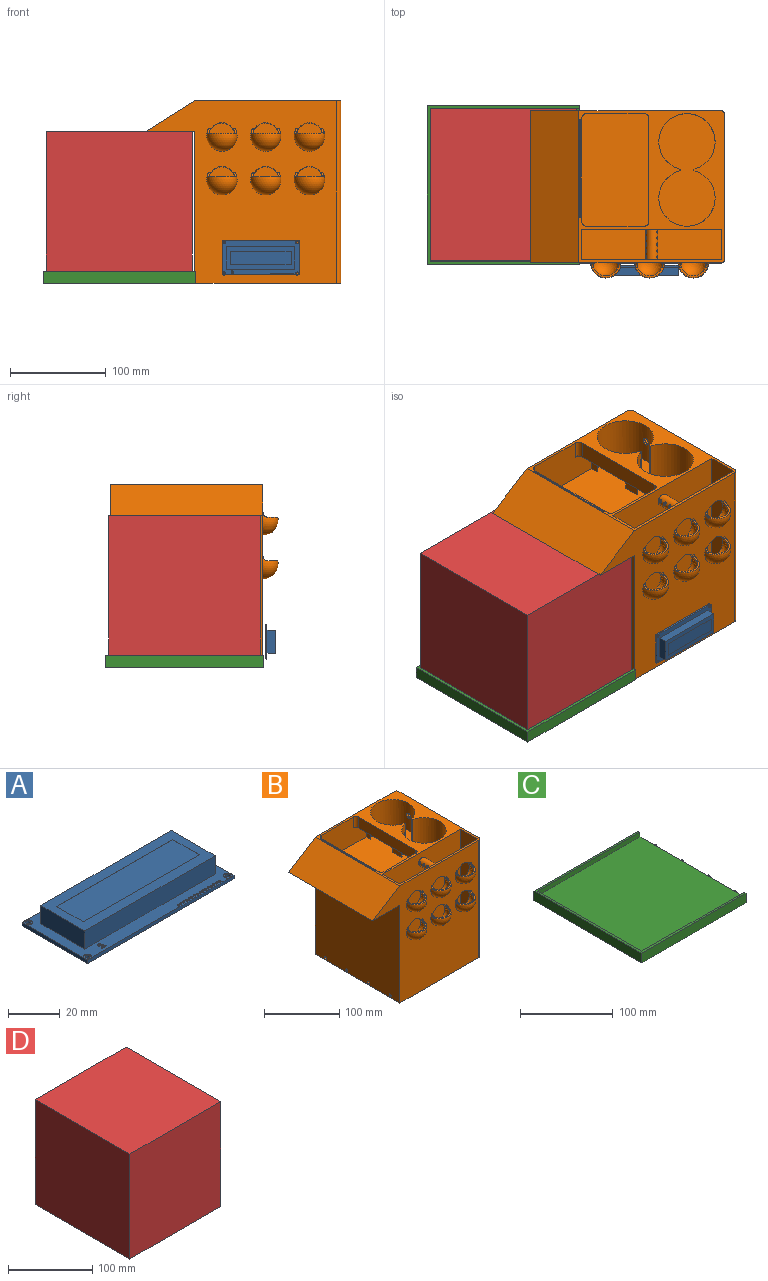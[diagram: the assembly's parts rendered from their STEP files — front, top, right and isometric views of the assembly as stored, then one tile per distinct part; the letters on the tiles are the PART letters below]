
ASSEMBLY  parts=4 mates=5
PART A: 160 faces, bbox 80.1x35.8x10.3 mm
  f0: plane 80.1x35.7mm, normal (0,0,1), area 1082mm2, adj f3,f4,f5,f6,f8,f9,f10,f11
  f1: plane 1.53x1.01mm, normal (0,0,1), area 0.4mm2, adj f5,f6,f22
  f2: plane 1.67x1.67mm, normal (0,0,1), area 0.6mm2, adj f4,f5,f18
  f3: plane 35.7x1.7mm, normal (1,0,0), area 60.7mm2, adj f0,f4,f6,f7
  f4: plane 80.1x1.7mm, normal (0,1,0), area 136.2mm2, adj f0,f2,f3,f5,f7
  f5: plane 35.7x1.7mm, normal (-1,0,0), area 60.7mm2, adj f0,f1,f2,f4,f6,f7
  f6: plane 80.1x1.7mm, normal (0,-1,0), area 136.2mm2, adj f0,f1,f3,f5,f7,f21,f26,f32
  f7: plane 80.1x35.7mm, normal (0,0,-1), area 2844.4mm2, adj f3,f4,f5,f6,f20,f29,f30,f31
  f8: plane 24x8.6mm, normal (1,0,0), area 206.4mm2, adj f0,f9,f11,f12
  f9: plane 71.2x8.6mm, normal (0,1,0), area 612.3mm2, adj f0,f8,f10,f12
  f10: plane 24x8.6mm, normal (-1,0,0), area 206.4mm2, adj f0,f9,f11,f12
  f11: plane 71.2x8.6mm, normal (0,-1,0), area 612.3mm2, adj f0,f8,f10,f12
  f12: plane 71.2x24mm, normal (0,0,1), area 802.2mm2, adj f8,f9,f10,f11,f13,f14,f15,f16
  f13: plane 14.3x0.05mm, normal (-1,0,0), area 0.7mm2, adj f12,f14,f16,f17
  f14: plane 63.4x0.05mm, normal (0,1,0), area 3.2mm2, adj f12,f13,f15,f17
  f15: plane 14.3x0.05mm, normal (1,0,0), area 0.7mm2, adj f12,f14,f16,f17
  f16: plane 63.4x0.05mm, normal (0,-1,0), area 3.2mm2, adj f12,f13,f15,f17
  f17: plane 63.4x14.3mm, normal (0,0,1), area 906.6mm2, adj f13,f14,f15,f16
  f18: cylinder r=1.67mm len=3.34mm, axis (0,0,-1), area 0mm2, adj f0,f2,f19
  f19: plane 3.34x3.34mm, normal (0,0,1), area 6mm2, adj f18,f20
  f20: cylinder r=0.94mm len=1.88mm, axis (0,0,1), area 10mm2, adj f7,f19
  f21: plane 1.33x0.14mm, normal (0,0,-1), area 0.1mm2, adj f6,f22
  f22: cylinder r=1.67mm len=3.34mm, axis (0,0,-1), area 0mm2, adj f0,f1,f21,f23
  f23: plane 3.34x3.34mm, normal (0,0,1), area 6mm2, adj f22,f29
  f24: cylinder r=1.67mm len=3.34mm, axis (0,0,-1), area 0mm2, adj f0,f25
  f25: plane 3.34x3.34mm, normal (0,0,1), area 6mm2, adj f24,f30
  f26: plane 1.33x0.14mm, normal (0,0,-1), area 0.1mm2, adj f6,f27
  f27: cylinder r=1.67mm len=3.34mm, axis (0,0,-1), area 0mm2, adj f0,f26,f28
  f28: plane 3.34x3.34mm, normal (0,0,1), area 6mm2, adj f27,f31
  f29: cylinder r=0.94mm len=1.88mm, axis (0,0,1), area 10mm2, adj f7,f23
  f30: cylinder r=0.94mm len=1.88mm, axis (0,0,1), area 10mm2, adj f7,f25
  f31: cylinder r=0.94mm len=1.88mm, axis (0,0,1), area 10mm2, adj f7,f28
  f32: plane 1.19x0mm, normal (1,0,0), area 0mm2, adj f0,f6,f33,f35
  f33: cylinder r=0.53mm len=1.06mm, axis (0,0,-1), area 0mm2, adj f0,f32,f34,f35
  f34: plane 1.19x0mm, normal (-1,0,0), area 0mm2, adj f0,f6,f33,f35
  f35: plane 1.72x1.06mm, normal (0,0,1), area 1.4mm2, adj f6,f32,f33,f34,f36
  f36: cylinder r=0.29mm len=1.7mm, axis (0,0,1), area 3.1mm2, adj f7,f35
  f37: plane 1.19x0mm, normal (1,0,0), area 0mm2, adj f0,f6,f38,f40
  f38: cylinder r=0.53mm len=1.06mm, axis (0,0,-1), area 0mm2, adj f0,f37,f39,f40
  f39: plane 1.19x0mm, normal (-1,0,0), area 0mm2, adj f0,f6,f38,f40
  f40: plane 1.72x1.06mm, normal (0,0,1), area 1.4mm2, adj f6,f37,f38,f39,f97
  f41: plane 1.19x0mm, normal (1,0,0), area 0mm2, adj f0,f6,f42,f44
  f42: cylinder r=0.53mm len=1.06mm, axis (0,0,-1), area 0mm2, adj f0,f41,f43,f44
  f43: plane 1.19x0mm, normal (-1,0,0), area 0mm2, adj f0,f6,f42,f44
  f44: plane 1.72x1.06mm, normal (0,0,1), area 1.4mm2, adj f6,f41,f42,f43,f98
  f45: plane 1.19x0mm, normal (1,0,0), area 0mm2, adj f0,f6,f46,f48
  f46: cylinder r=0.53mm len=1.06mm, axis (0,0,-1), area 0mm2, adj f0,f45,f47,f48
  f47: plane 1.19x0mm, normal (-1,0,0), area 0mm2, adj f0,f6,f46,f48
  f48: plane 1.72x1.06mm, normal (0,0,1), area 1.4mm2, adj f6,f45,f46,f47,f99
  f49: plane 1.19x0mm, normal (1,0,0), area 0mm2, adj f0,f6,f50,f52
  f50: cylinder r=0.53mm len=1.06mm, axis (0,0,-1), area 0mm2, adj f0,f49,f51,f52
  f51: plane 1.19x0mm, normal (-1,0,0), area 0mm2, adj f0,f6,f50,f52
  f52: plane 1.72x1.06mm, normal (0,0,1), area 1.4mm2, adj f6,f49,f50,f51,f100
  f53: plane 1.19x0mm, normal (1,0,0), area 0mm2, adj f0,f6,f54,f56
  f54: cylinder r=0.53mm len=1.06mm, axis (0,0,-1), area 0mm2, adj f0,f53,f55,f56
  f55: plane 1.19x0mm, normal (-1,0,0), area 0mm2, adj f0,f6,f54,f56
  f56: plane 1.72x1.06mm, normal (0,0,1), area 1.4mm2, adj f6,f53,f54,f55,f101
  f57: plane 1.19x0mm, normal (1,0,0), area 0mm2, adj f0,f6,f58,f60
  f58: cylinder r=0.53mm len=1.06mm, axis (0,0,-1), area 0mm2, adj f0,f57,f59,f60
  f59: plane 1.19x0mm, normal (-1,0,0), area 0mm2, adj f0,f6,f58,f60
  f60: plane 1.72x1.06mm, normal (0,0,1), area 1.4mm2, adj f6,f57,f58,f59,f102
  f61: plane 1.19x0mm, normal (1,0,0), area 0mm2, adj f0,f6,f62,f64
  f62: cylinder r=0.53mm len=1.06mm, axis (0,0,-1), area 0mm2, adj f0,f61,f63,f64
  f63: plane 1.19x0mm, normal (-1,0,0), area 0mm2, adj f0,f6,f62,f64
  f64: plane 1.72x1.06mm, normal (0,0,1), area 1.4mm2, adj f6,f61,f62,f63,f103
  f65: plane 1.19x0mm, normal (1,0,0), area 0mm2, adj f0,f6,f66,f68
  f66: cylinder r=0.53mm len=1.06mm, axis (0,0,-1), area 0mm2, adj f0,f65,f67,f68
  f67: plane 1.19x0mm, normal (-1,0,0), area 0mm2, adj f0,f6,f66,f68
  f68: plane 1.72x1.06mm, normal (0,0,1), area 1.4mm2, adj f6,f65,f66,f67,f104
  f69: plane 1.19x0mm, normal (1,0,0), area 0mm2, adj f0,f6,f70,f72
  f70: cylinder r=0.53mm len=1.06mm, axis (0,0,-1), area 0mm2, adj f0,f69,f71,f72
  f71: plane 1.19x0mm, normal (-1,0,0), area 0mm2, adj f0,f6,f70,f72
  f72: plane 1.72x1.06mm, normal (0,0,1), area 1.4mm2, adj f6,f69,f70,f71,f105
  f73: plane 1.19x0mm, normal (1,0,0), area 0mm2, adj f0,f6,f74,f76
  f74: cylinder r=0.53mm len=1.06mm, axis (0,0,-1), area 0mm2, adj f0,f73,f75,f76
  f75: plane 1.19x0mm, normal (-1,0,0), area 0mm2, adj f0,f6,f74,f76
  f76: plane 1.72x1.06mm, normal (0,0,1), area 1.4mm2, adj f6,f73,f74,f75,f106
  f77: plane 1.19x0mm, normal (1,0,0), area 0mm2, adj f0,f6,f78,f80
  f78: cylinder r=0.53mm len=1.06mm, axis (0,0,-1), area 0mm2, adj f0,f77,f79,f80
  f79: plane 1.19x0mm, normal (-1,0,0), area 0mm2, adj f0,f6,f78,f80
  f80: plane 1.72x1.06mm, normal (0,0,1), area 1.4mm2, adj f6,f77,f78,f79,f107
  f81: plane 1.19x0mm, normal (1,0,0), area 0mm2, adj f0,f6,f82,f84
  f82: cylinder r=0.53mm len=1.06mm, axis (0,0,-1), area 0mm2, adj f0,f81,f83,f84
  f83: plane 1.19x0mm, normal (-1,0,0), area 0mm2, adj f0,f6,f82,f84
  f84: plane 1.72x1.06mm, normal (0,0,1), area 1.4mm2, adj f6,f81,f82,f83,f108
  f85: plane 1.19x0mm, normal (1,0,0), area 0mm2, adj f0,f6,f86,f88
  f86: cylinder r=0.53mm len=1.06mm, axis (0,0,-1), area 0mm2, adj f0,f85,f87,f88
  f87: plane 1.19x0mm, normal (-1,0,0), area 0mm2, adj f0,f6,f86,f88
  f88: plane 1.72x1.06mm, normal (0,0,1), area 1.4mm2, adj f6,f85,f86,f87,f109
  f89: plane 1.19x0mm, normal (1,0,0), area 0mm2, adj f0,f6,f90,f92
  f90: cylinder r=0.53mm len=1.06mm, axis (0,0,-1), area 0mm2, adj f0,f89,f91,f92
  f91: plane 1.19x0mm, normal (-1,0,0), area 0mm2, adj f0,f6,f90,f92
  f92: plane 1.72x1.06mm, normal (0,0,1), area 1.4mm2, adj f6,f89,f90,f91,f110
  f93: plane 1.19x0mm, normal (1,0,0), area 0mm2, adj f0,f6,f94,f96
  f94: cylinder r=0.53mm len=1.06mm, axis (0,0,-1), area 0mm2, adj f0,f93,f95,f96
  f95: plane 1.19x0mm, normal (-1,0,0), area 0mm2, adj f0,f6,f94,f96
  f96: plane 1.72x1.06mm, normal (0,0,1), area 1.4mm2, adj f6,f93,f94,f95,f111
  f97: cylinder r=0.29mm len=1.7mm, axis (0,0,1), area 3.1mm2, adj f7,f40
  f98: cylinder r=0.29mm len=1.7mm, axis (0,0,1), area 3.1mm2, adj f7,f44
  f99: cylinder r=0.29mm len=1.7mm, axis (0,0,1), area 3.1mm2, adj f7,f48
  f100: cylinder r=0.29mm len=1.7mm, axis (0,0,1), area 3.1mm2, adj f7,f52
  f101: cylinder r=0.29mm len=1.7mm, axis (0,0,1), area 3.1mm2, adj f7,f56
  f102: cylinder r=0.29mm len=1.7mm, axis (0,0,1), area 3.1mm2, adj f7,f60
  f103: cylinder r=0.29mm len=1.7mm, axis (0,0,1), area 3.1mm2, adj f7,f64
  f104: cylinder r=0.29mm len=1.7mm, axis (0,0,1), area 3.1mm2, adj f7,f68
  f105: cylinder r=0.29mm len=1.7mm, axis (0,0,1), area 3.1mm2, adj f7,f72
  f106: cylinder r=0.29mm len=1.7mm, axis (0,0,1), area 3.1mm2, adj f7,f76
  f107: cylinder r=0.29mm len=1.7mm, axis (0,0,1), area 3.1mm2, adj f7,f80
  f108: cylinder r=0.29mm len=1.7mm, axis (0,0,1), area 3.1mm2, adj f7,f84
  f109: cylinder r=0.29mm len=1.7mm, axis (0,0,1), area 3.1mm2, adj f7,f88
  f110: cylinder r=0.29mm len=1.7mm, axis (0,0,1), area 3.1mm2, adj f7,f92
  f111: cylinder r=0.29mm len=1.7mm, axis (0,0,1), area 3.1mm2, adj f7,f96
  f112: cylinder r=0.46mm len=0.14mm, axis (0,0,-1), area 0mm2, adj f113,f155,f156,f159
  f113: cylinder r=0.42mm len=0.18mm, axis (0,0,-1), area 0mm2, adj f112,f114,f156,f159
  f114: cylinder r=1.01mm len=0.33mm, axis (0,0,-1), area 0mm2, adj f113,f115,f156,f159
  f115: plane 0.11x0.1mm, normal (0.38,0.93,0), area 0mm2, adj f114,f116,f156,f159
  f116: plane 0.43x0.16mm, normal (-0.93,0.36,0), area 0mm2, adj f115,f117,f156,f159
  f117: plane 0.47x0.15mm, normal (-0.95,0.31,0), area 0mm2, adj f116,f118,f156,f159
  f118: cylinder r=0.82mm len=0.1mm, axis (0,0,-1), area 0mm2, adj f117,f119,f156,f159
  f119: cylinder r=0.71mm len=0.28mm, axis (0,0,-1), area 0mm2, adj f118,f120,f156,f159
  f120: extruded ~0.37x0.11mm, area 0mm2, adj f119,f155,f156,f159
  f121: extruded ~0.17x0.1mm, area 0mm2, adj f122,f152,f156,f158
  f122: plane 0.49x0.18mm, normal (0.94,-0.34,0), area 0.1mm2, adj f121,f123,f156,f158
  f123: cylinder r=0.59mm len=0.12mm, axis (0,0,-1), area 0mm2, adj f122,f152,f156,f158
  f124: cylinder r=2.75mm len=0.28mm, axis (0,0,1), area 0mm2, adj f125,f153,f156,f157
  f125: cylinder r=1.46mm len=0.25mm, axis (0,0,1), area 0mm2, adj f124,f126,f156,f157
  f126: cylinder r=0.53mm len=0.1mm, axis (0,0,1), area 0mm2, adj f125,f127,f156,f157
  f127: plane 1.13x0.34mm, normal (0.96,0.29,0), area 0.1mm2, adj f126,f128,f156,f157
  f128: plane 0.75x0.31mm, normal (-0.92,0.38,0), area 0.1mm2, adj f127,f153,f156,f157
  f129: plane 0.2x0.1mm, normal (0.92,-0.39,0), area 0mm2, adj f0,f130,f154,f156
  f130: extruded ~0.32x0.26mm, area 0mm2, adj f0,f129,f131,f156
  f131: extruded ~0.31x0.25mm, area 0mm2, adj f0,f130,f132,f156
  f132: plane 2.73x0.95mm, normal (-0.94,-0.33,0), area 0.3mm2, adj f0,f131,f133,f156
  f133: plane 0.1x0.04mm, normal (-0.97,-0.23,0), area 0mm2, adj f0,f132,f134,f156
  f134: extruded ~0.14x0.11mm, area 0mm2, adj f0,f133,f135,f156
  f135: cylinder r=0.51mm len=0.24mm, axis (0,0,1), area 0mm2, adj f0,f134,f136,f156
  f136: extruded ~0.19x0.1mm, area 0mm2, adj f0,f135,f137,f156
  f137: plane 0.58x0.2mm, normal (0.94,0.33,0), area 0.1mm2, adj f0,f136,f138,f156
  f138: plane 0.1x0.03mm, normal (-1,-0.04,0), area 0mm2, adj f0,f137,f139,f156
  f139: extruded ~0.63x0.25mm, area 0.1mm2, adj f0,f138,f140,f156
  f140: extruded ~0.67x0.22mm, area 0.1mm2, adj f0,f139,f141,f156
  f141: extruded ~0.63x0.15mm, area 0.1mm2, adj f0,f140,f142,f156
  f142: cylinder r=0.76mm len=0.18mm, axis (0,0,1), area 0mm2, adj f0,f141,f143,f156
  f143: plane 0.1x0.01mm, normal (0.46,0.89,0), area 0mm2, adj f0,f142,f144,f156
  f144: extruded ~0.13x0.1mm, area 0mm2, adj f0,f143,f145,f156
  f145: plane 0.1x0.04mm, normal (0.99,-0.13,0), area 0mm2, adj f0,f144,f146,f156
  f146: plane 1.11x0.41mm, normal (0.94,-0.34,0), area 0.1mm2, adj f0,f145,f147,f156
  f147: cylinder r=0.89mm len=0.17mm, axis (0,0,1), area 0mm2, adj f0,f146,f148,f156
  f148: extruded ~0.44x0.14mm, area 0mm2, adj f0,f147,f149,f156
  f149: cylinder r=0.76mm len=0.37mm, axis (0,0,1), area 0mm2, adj f0,f148,f150,f156
  f150: cylinder r=0.6mm len=0.24mm, axis (0,0,1), area 0mm2, adj f0,f149,f151,f156
  f151: cylinder r=1.08mm len=0.3mm, axis (0,0,1), area 0mm2, adj f0,f150,f154,f156
  f152: cylinder r=0.32mm len=0.27mm, axis (0,0,-1), area 0mm2, adj f121,f123,f156,f158
  f153: plane 0.1x0.04mm, normal (-0.36,-0.93,0), area 0mm2, adj f124,f128,f156,f157
  f154: cylinder r=1.34mm len=0.2mm, axis (0,0,1), area 0mm2, adj f0,f129,f151,f156
  f155: extruded ~0.32x0.14mm, area 0mm2, adj f112,f120,f156,f159
  f156: plane 3.41x2.58mm, normal (0,0,1), area 4.8mm2, adj f112,f113,f114,f115,f116,f117,f118,f119
  f157: plane 1.13x0.65mm, normal (0,0,1), area 0.3mm2, adj f124,f125,f126,f127,f128,f153
  f158: plane 0.49x0.26mm, normal (0,0,1), area 0.1mm2, adj f121,f122,f123,f152
  f159: plane 0.99x0.89mm, normal (0,0,1), area 0.6mm2, adj f112,f113,f114,f115,f116,f117,f118,f119
PART B: 95 faces, bbox 203.2x174.6x190.5 mm
  f0: cylinder r=3.91mm len=7.83mm, axis (1,0,0), area 67.5mm2, adj f6,f93
  f1: plane 158.75x152.4mm, normal (0,0,1), area 5716.6mm2, adj f4,f6,f7,f8,f9,f10,f13,f14
  f2: cylinder r=6.23mm len=32mm, axis (0,1,0), area 1089.1mm2, adj f4,f13,f33,f34,f35,f36,f37,f38
  f3: cylinder r=4.95mm len=38.1mm, axis (0,-1,0), area 1046.4mm2, adj f5,f19,f23,f28,f31,f32,f33,f34
  f4: plane 152.4x146.3mm, normal (0,-1,0), area 22174.8mm2, adj f1,f2,f14,f15,f16
  f5: plane 3.53x1.42mm, normal (0,0,-1), area 1.6mm2, adj f3,f19,f28
  f6: cylinder r=29.4mm len=58.8mm, axis (0,0,1), area 6258.3mm2, adj f0,f1,f17,f18,f23,f24,f25,f94
  f7: cylinder r=29.4mm len=58.8mm, axis (0,0,1), area 6306.6mm2, adj f1,f17,f18,f23,f24,f26,f94
  f8: plane 198.63x190.5mm, normal (0,-1,0), area 24579.4mm2, adj f1,f11,f12,f51,f52,f53,f54,f55
  f9: plane 190.5x149.61mm, normal (1,0,0), area 28426.8mm2, adj f1,f12,f85,f86,f92
  f10: plane 198.63x190.5mm, normal (0,1,0), area 28967.7mm2, adj f1,f11,f12,f51,f52,f86
  f11: plane 158.75x158.75mm, normal (-1,0,0), area 25146.4mm2, adj f8,f10,f12,f43,f45,f47,f49,f51
  f12: plane 158.75x152.4mm, normal (0,0,-1), area 24184.5mm2, adj f8,f9,f10,f11,f85,f86
  f13: plane 152.4x146.3mm, normal (0,1,0), area 18740.9mm2, adj f1,f2,f14,f15,f16,f60,f62,f63
  f14: plane 152.4x32mm, normal (-1,0,0), area 4877.4mm2, adj f1,f4,f13,f16
  f15: plane 152.4x32mm, normal (1,0,0), area 4877.4mm2, adj f1,f4,f13,f16
  f16: plane 146.3x32mm, normal (0,0,1), area 4682.3mm2, adj f4,f13,f14,f15
  f17: cylinder r=0.95mm len=44.45mm, axis (0,0,1), area 111.8mm2, adj f1,f6,f7,f94
  f18: cylinder r=0.95mm len=44.45mm, axis (0,0,1), area 111.8mm2, adj f1,f6,f7,f94
  f19: plane 84.07x44.45mm, normal (0,1,0), area 3287.2mm2, adj f1,f3,f5,f23,f26,f28,f29,f94
  f20: plane 107.44x17.78mm, normal (-1,0,0), area 1910.3mm2, adj f1,f23,f27,f28
  f21: plane 84.07x44.45mm, normal (0,-1,0), area 3308.1mm2, adj f1,f23,f25,f27,f30,f94
  f22: plane 107.44x44.45mm, normal (1,0,0), area 4775.8mm2, adj f1,f29,f30,f94
  f23: plane 117.6x24.13mm, normal (0,0,-1), area 1711.4mm2, adj f3,f6,f7,f19,f20,f21,f24,f25
  f24: plane 26.67x16.8mm, normal (-1,0,0), area 448mm2, adj f6,f7,f23,f94
  f25: plane 26.67x8.4mm, normal (-1,0,0), area 224mm2, adj f6,f21,f23,f94
  f26: plane 26.67x8.4mm, normal (-1,0,0), area 224mm2, adj f7,f19,f23,f94
  f27: cylinder r=5.08mm len=17.78mm, axis (0,0,-1), area 141.9mm2, adj f1,f20,f21,f23
  f28: cylinder r=5.08mm len=17.78mm, axis (0,0,-1), area 131.4mm2, adj f1,f3,f5,f19,f20,f23,f31
  f29: cylinder r=5.08mm len=44.45mm, axis (0,0,1), area 354.7mm2, adj f1,f19,f22,f94
  f30: cylinder r=5.08mm len=44.45mm, axis (0,0,1), area 354.7mm2, adj f1,f21,f22,f94
  f31: plane 8.42x6.77mm, normal (0,-1,0), area 50.1mm2, adj f3,f23,f28
  f32: plane 9.9x9.9mm, normal (0,1,0), area 77mm2, adj f3
  f33: cylinder r=1.65mm len=3.3mm, axis (-1,0,0), area 14.5mm2, adj f2,f3
  f34: cylinder r=1.65mm len=3.3mm, axis (-1,0,0), area 14.5mm2, adj f2,f3
  f35: cylinder r=1.65mm len=3.3mm, axis (-1,0,0), area 14.5mm2, adj f2,f3
  f36: cylinder r=1.65mm len=3.3mm, axis (-1,0,0), area 14.5mm2, adj f2,f3
  f37: cylinder r=1.65mm len=3.3mm, axis (-1,0,0), area 14.5mm2, adj f2,f3
  f38: cylinder r=1.65mm len=3.3mm, axis (-1,0,0), area 14.5mm2, adj f2,f3
  f39: cylinder r=1.65mm len=3.3mm, axis (-1,0,0), area 14.5mm2, adj f2,f3
  f40: cylinder r=1.65mm len=3.3mm, axis (-1,0,0), area 14.5mm2, adj f2,f3
  f41: cylinder r=1.65mm len=3.3mm, axis (-1,0,0), area 14.5mm2, adj f2,f3
  f42: cylinder r=1.65mm len=3.3mm, axis (-1,0,0), area 14.5mm2, adj f2,f3
  f43: cylinder r=2.1mm len=4.19mm, axis (-1,0,0), area 50.2mm2, adj f11,f44
  f44: plane 4.19x4.19mm, normal (-1,0,0), area 13.8mm2, adj f43
  f45: cylinder r=2.1mm len=4.19mm, axis (-1,0,0), area 50.2mm2, adj f11,f46
  f46: plane 4.19x4.19mm, normal (-1,0,0), area 13.8mm2, adj f45
  f47: cylinder r=2.1mm len=4.19mm, axis (-1,0,0), area 50.2mm2, adj f11,f48
  f48: plane 4.19x4.19mm, normal (-1,0,0), area 13.8mm2, adj f47
  f49: cylinder r=2.1mm len=4.19mm, axis (-1,0,0), area 50.2mm2, adj f11,f50
  f50: plane 4.19x4.19mm, normal (-1,0,0), area 13.8mm2, adj f49
  f51: plane 158.75x50.8mm, normal (0,0,-1), area 8064.5mm2, adj f8,f10,f11,f52
  f52: plane 158.75x50.8mm, normal (-0.53,0,0.85), area 9510mm2, adj f1,f8,f10,f51
  f53: sphere r=15.88mm, area 950.6mm2, adj f8,f59,f73,f74
  f54: sphere r=15.88mm, area 950.6mm2, adj f8,f68,f83,f84
  f55: sphere r=15.88mm, area 950.6mm2, adj f8,f69,f81,f82
  f56: sphere r=15.88mm, area 950.6mm2, adj f8,f70,f79,f80
  f57: sphere r=15.88mm, area 950.6mm2, adj f8,f71,f77,f78
  f58: sphere r=15.88mm, area 950.6mm2, adj f8,f72,f75,f76
  f59: plane 29.5x10.52mm, normal (0,0,1), area 73.3mm2, adj f53,f60,f73,f74
  f60: sphere r=13.84mm, area 1007.4mm2, adj f8,f13,f59,f73,f74
  f61: plane 5.38x0.99mm, normal (0,-1,0), area 3.1mm2, adj f2,f62
  f62: cylinder r=15.58mm len=13.21mm, axis (0,-1,0), area 71.9mm2, adj f2,f13,f61
  f63: sphere r=13.84mm, area 1007.4mm2, adj f8,f13,f68,f83,f84
  f64: sphere r=13.84mm, area 1007.4mm2, adj f8,f13,f69,f81,f82
  f65: sphere r=13.84mm, area 1007.4mm2, adj f8,f13,f70,f79,f80
  f66: sphere r=13.84mm, area 1007.4mm2, adj f8,f13,f71,f77,f78
  f67: sphere r=13.84mm, area 1007.4mm2, adj f8,f13,f72,f75,f76
  f68: plane 29.5x10.52mm, normal (0,0,1), area 73.3mm2, adj f54,f63,f83,f84
  f69: plane 29.5x10.52mm, normal (0,0,1), area 73.3mm2, adj f55,f64,f81,f82
  f70: plane 29.5x10.52mm, normal (0,0,1), area 73.3mm2, adj f56,f65,f79,f80
  f71: plane 29.5x10.52mm, normal (0,0,1), area 73.3mm2, adj f57,f66,f77,f78
  f72: plane 29.5x10.52mm, normal (0,0,1), area 73.3mm2, adj f58,f67,f75,f76
  f73: cylinder r=5.08mm len=5.08mm, axis (-1,0,0), area 17.5mm2, adj f8,f53,f59,f60
  f74: cylinder r=5.08mm len=5.08mm, axis (-1,0,0), area 17.5mm2, adj f8,f53,f59,f60
  f75: cylinder r=5.08mm len=5.08mm, axis (-1,0,0), area 17.5mm2, adj f8,f58,f67,f72
  f76: cylinder r=5.08mm len=5.08mm, axis (-1,0,0), area 17.5mm2, adj f8,f58,f67,f72
  f77: cylinder r=5.08mm len=5.08mm, axis (-1,0,0), area 17.5mm2, adj f8,f57,f66,f71
  f78: cylinder r=5.08mm len=5.08mm, axis (-1,0,0), area 17.5mm2, adj f8,f57,f66,f71
  f79: cylinder r=5.08mm len=5.08mm, axis (-1,0,0), area 17.5mm2, adj f8,f56,f65,f70
  f80: cylinder r=5.08mm len=5.08mm, axis (-1,0,0), area 17.5mm2, adj f8,f56,f65,f70
  f81: cylinder r=5.08mm len=5.08mm, axis (-1,0,0), area 17.5mm2, adj f8,f55,f64,f69
  f82: cylinder r=5.08mm len=5.08mm, axis (-1,0,0), area 17.5mm2, adj f8,f55,f64,f69
  f83: cylinder r=5.08mm len=5.08mm, axis (-1,0,0), area 17.5mm2, adj f8,f54,f63,f68
  f84: cylinder r=5.08mm len=5.08mm, axis (-1,0,0), area 17.5mm2, adj f8,f54,f63,f68
  f85: cylinder r=4.57mm len=190.5mm, axis (0,0,1), area 1368.1mm2, adj f1,f8,f9,f12
  f86: cylinder r=4.57mm len=190.5mm, axis (0,0,-1), area 1368.1mm2, adj f1,f9,f10,f12
  f87: plane 103.07x25.4mm, normal (1,0,0), area 2617.9mm2, adj f1,f88,f90,f91
  f88: plane 25.4x1.22mm, normal (0,1,0), area 30.9mm2, adj f1,f87,f89,f91
  f89: plane 103.07x25.4mm, normal (-1,0,0), area 2617.9mm2, adj f1,f88,f90,f91
  f90: plane 25.4x1.22mm, normal (0,-1,0), area 30.9mm2, adj f1,f87,f89,f91
  f91: plane 103.07x1.22mm, normal (0,0,1), area 125.3mm2, adj f87,f88,f89,f90
  f92: cylinder r=4.83mm len=9.65mm, axis (1,0,0), area 231.1mm2, adj f9,f93
  f93: plane 9.65x9.65mm, normal (1,0,0), area 25.1mm2, adj f0,f92
  f94: plane 139.13x117.6mm, normal (0,0,1), area 15400.3mm2, adj f6,f7,f17,f18,f19,f21,f22,f24
PART C: 18 faces, bbox 162.3x165.1x12.7 mm
  f0: plane 155.96x6.35mm, normal (0,-1,0), area 990.3mm2, adj f1,f4,f5,f9
  f1: plane 159x155.96mm, normal (0,0,1), area 24797.6mm2, adj f0,f3,f4,f5
  f2: plane 165.1x159mm, normal (0,0,-1), area 26251.6mm2, adj f5,f6,f7,f8
  f3: plane 155.96x6.35mm, normal (0,1,0), area 990.3mm2, adj f1,f4,f5,f9
  f4: plane 159x6.35mm, normal (1,0,0), area 1009.7mm2, adj f0,f1,f3,f9
  f5: plane 165.1x12.7mm, normal (1,0,0), area 1041.5mm2, adj f0,f1,f2,f3,f6,f8,f9,f11
  f6: plane 159x12.7mm, normal (0,1,0), area 2019.4mm2, adj f2,f5,f7,f9
  f7: plane 165.1x12.7mm, normal (-1,0,0), area 2096.8mm2, adj f2,f6,f8,f9
  f8: plane 159x12.7mm, normal (0,-1,0), area 2019.4mm2, adj f2,f5,f7,f9
  f9: plane 165.1x159mm, normal (0,0,1), area 1453.9mm2, adj f0,f3,f4,f5,f6,f7,f8
  f10: plane 3.81x3.81mm, normal (1,0,0), area 11.4mm2, adj f11
  f11: cylinder r=1.91mm len=3.81mm, axis (-1,0,0), area 39.5mm2, adj f5,f10
  f12: plane 3.81x3.81mm, normal (1,0,0), area 11.4mm2, adj f13
  f13: cylinder r=1.91mm len=3.81mm, axis (-1,0,0), area 39.5mm2, adj f5,f12
  f14: plane 3.81x3.81mm, normal (1,0,0), area 11.4mm2, adj f15
  f15: cylinder r=1.91mm len=3.81mm, axis (-1,0,0), area 39.5mm2, adj f5,f14
  f16: plane 3.81x3.81mm, normal (1,0,0), area 11.4mm2, adj f17
  f17: cylinder r=1.91mm len=3.81mm, axis (-1,0,0), area 39.5mm2, adj f5,f16
PART D: 6 faces, bbox 152.7x158.8x152.4 mm
  f0: plane 152.65x152.4mm, normal (0,-1,0), area 23264.5mm2, adj f1,f3,f4,f5
  f1: plane 158.75x152.4mm, normal (1,0,0), area 24193.5mm2, adj f0,f2,f4,f5
  f2: plane 152.65x152.4mm, normal (0,1,0), area 23264.5mm2, adj f1,f3,f4,f5
  f3: plane 158.75x152.4mm, normal (-1,0,0), area 24193.5mm2, adj f0,f2,f4,f5
  f4: plane 158.75x152.65mm, normal (0,0,1), area 24233.8mm2, adj f0,f1,f2,f3
  f5: plane 158.75x152.65mm, normal (0,0,-1), area 24233.8mm2, adj f0,f1,f2,f3
PLACE A rot(axis=(1,0,0),90deg) t=(27.76,-19.57,-5.91)mm
PLACE B t=(35.28,62.29,-32.37)mm
PLACE C t=(-119.91,64.41,-32.37)mm
PLACE D rot(axis=(1,0,0),180deg) t=(-120.04,64.54,126.38)mm
MATE planar D.f0 <-> C.f0  axis (0,1,0) through (-120.04,143.91,50.18)mm
MATE parallel A.f7 <-> B.f8  axis (0,1,0) through (27.73,-19.57,-5.88)mm
MATE planar D.f4 <-> C.f1  axis (0,0,-1) through (-120.04,64.54,-26.02)mm
MATE planar D.f3 <-> C.f4  axis (-1,0,0) through (-196.37,64.54,50.18)mm
MATE fastened C.f17 <-> B.f43  axis (1,0,0) through (-37.11,1.33,-29.19)mm
